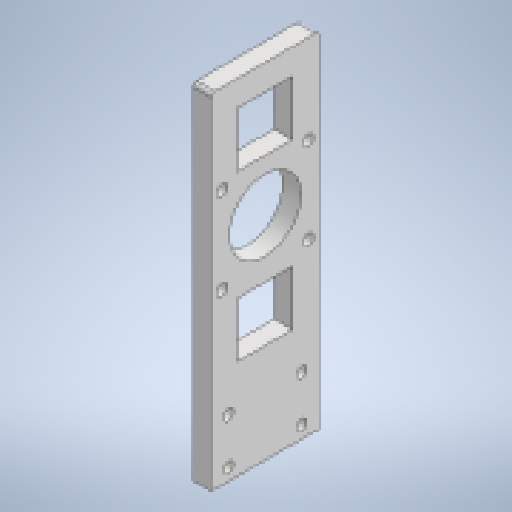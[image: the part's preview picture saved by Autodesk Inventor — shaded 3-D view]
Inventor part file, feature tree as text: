
AUTODESK INVENTOR PART (.ipt)
format: ipt  version: 2023 (Build 270158000, 158)  size: 189,952 bytes
history: native  units: mm
features: extrude x3, sketch x3
ambient origin geometry x8: Origin, YZ Plane, XZ Plane, XY Plane, X Axis, Y Axis, Z Axis, Center Point
bodies: Solid1 (feature_tree)
feature tree (6):
  extrude  "Extrusion1"  Depth=25.0mm
  extrude  "Extrusion2"  Depth=58.8mm
  extrude  "Extrusion3"  Depth=10.0mm TaperAngle=0.0deg
  sketch  "Sketch1"  dims[d0=6.0mm d1=25.0mm]
  sketch  "Sketch3"  dims[d2=40.0mm d3=58.8mm]
  sketch  "Sketch4"  dims[d4=38.2mm d5=10.0mm d6=0.0mm d7=150.0mm d8=2.0mm d9=30.0mm d12=60.0mm d13=16.0mm d14=10.0mm d15=0.0mm d16=47.14mm d17=6.0mm d18=56.4mm d19=39.0mm d20=20.0mm d21=0.0mm]
